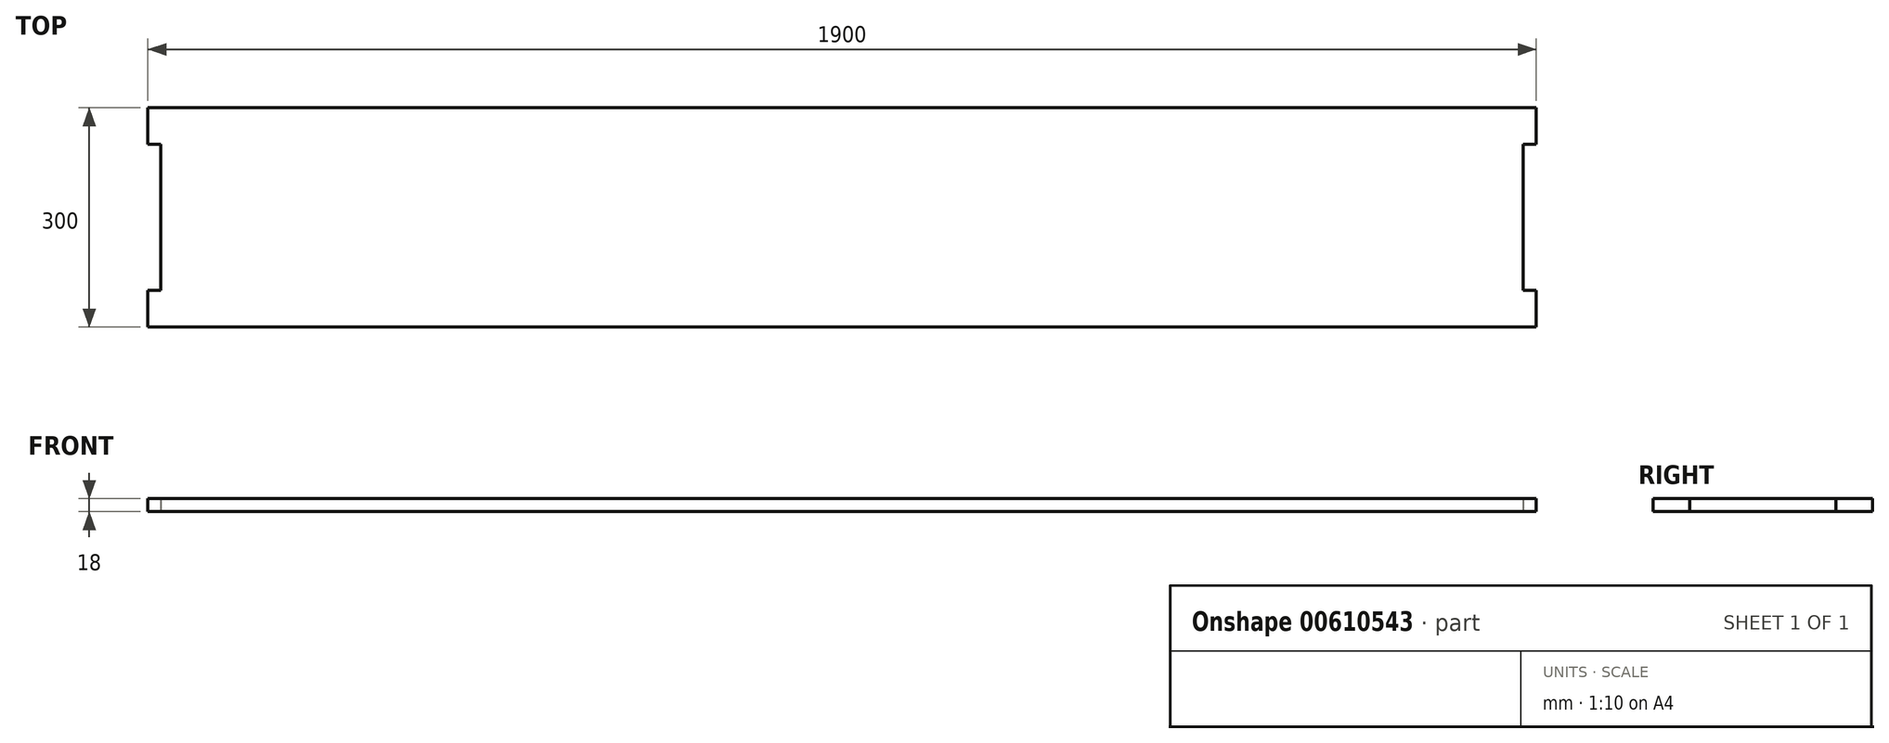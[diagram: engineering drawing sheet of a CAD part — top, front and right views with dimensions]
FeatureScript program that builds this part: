
annotation { "Feature Type Name" : "Feature", "Feature Type Description" : "" }
export const myFeature = defineFeature(function(context is Context, id is Id, definition is map)
    precondition{}
    {
        {
            var Q0;
            Q0=qCreatedBy(makeId("Top.planeOp"),FACE);
            var sketch = newSketch(context, id + "F0", { "sketchPlane" : qUnion([Q0])});
            skLineSegment(sketch, "E0.bottom", {"start": v(0, 0) * mm, "end": v(1900, 0) * mm});
            skLineSegment(sketch, "E0.top", {"start": v(0, 300) * mm, "end": v(1900, 300) * mm});
            skLineSegment(sketch, "E0.left", {"start": v(0, 0) * mm, "end": v(0, 50) * mm});
            skLineSegment(sketch, "E0.right", {"start": v(1900, 0) * mm, "end": v(1900, 50) * mm});
            skLineSegment(sketch, "E1.bottom", {"start": v(0, 250) * mm, "end": v(18, 250) * mm});
            skLineSegment(sketch, "E1.top", {"start": v(0, 50) * mm, "end": v(18, 50) * mm});
            skLineSegment(sketch, "E1.right", {"start": v(18, 250) * mm, "end": v(18, 50) * mm});
            skLineSegment(sketch, "E2.bottom", {"start": v(1900, 250) * mm, "end": v(1882, 250) * mm});
            skLineSegment(sketch, "E2.top", {"start": v(1900, 50) * mm, "end": v(1882, 50) * mm});
            skLineSegment(sketch, "E2.right", {"start": v(1882, 250) * mm, "end": v(1882, 50) * mm});
            skLineSegment(sketch, "E3.trimOffspring", {"start": v(0, 250) * mm, "end": v(0, 300) * mm});
            skLineSegment(sketch, "E4.trimOffspring", {"start": v(1900, 250) * mm, "end": v(1900, 300) * mm});
            skSolve(sketch);
        }
        {
            var Q0;
            Q0=makeQuery(id+"F0.imprint","IMPRINT",FACE,{"disambiguationData":[TD([[makeQuery(id+"F0.imprint","IMPRINT",EDGE,{"derivedFrom":sQuery(id+"F0.wireOp",EDGE,"E0.bottom")}),1.0]])]});
            extrude(context, id + "F1", {"entities" : qUnion([Q0]), "depth" : 18 * mm, "offsetDistance" : 25 * mm});
        }
    });
